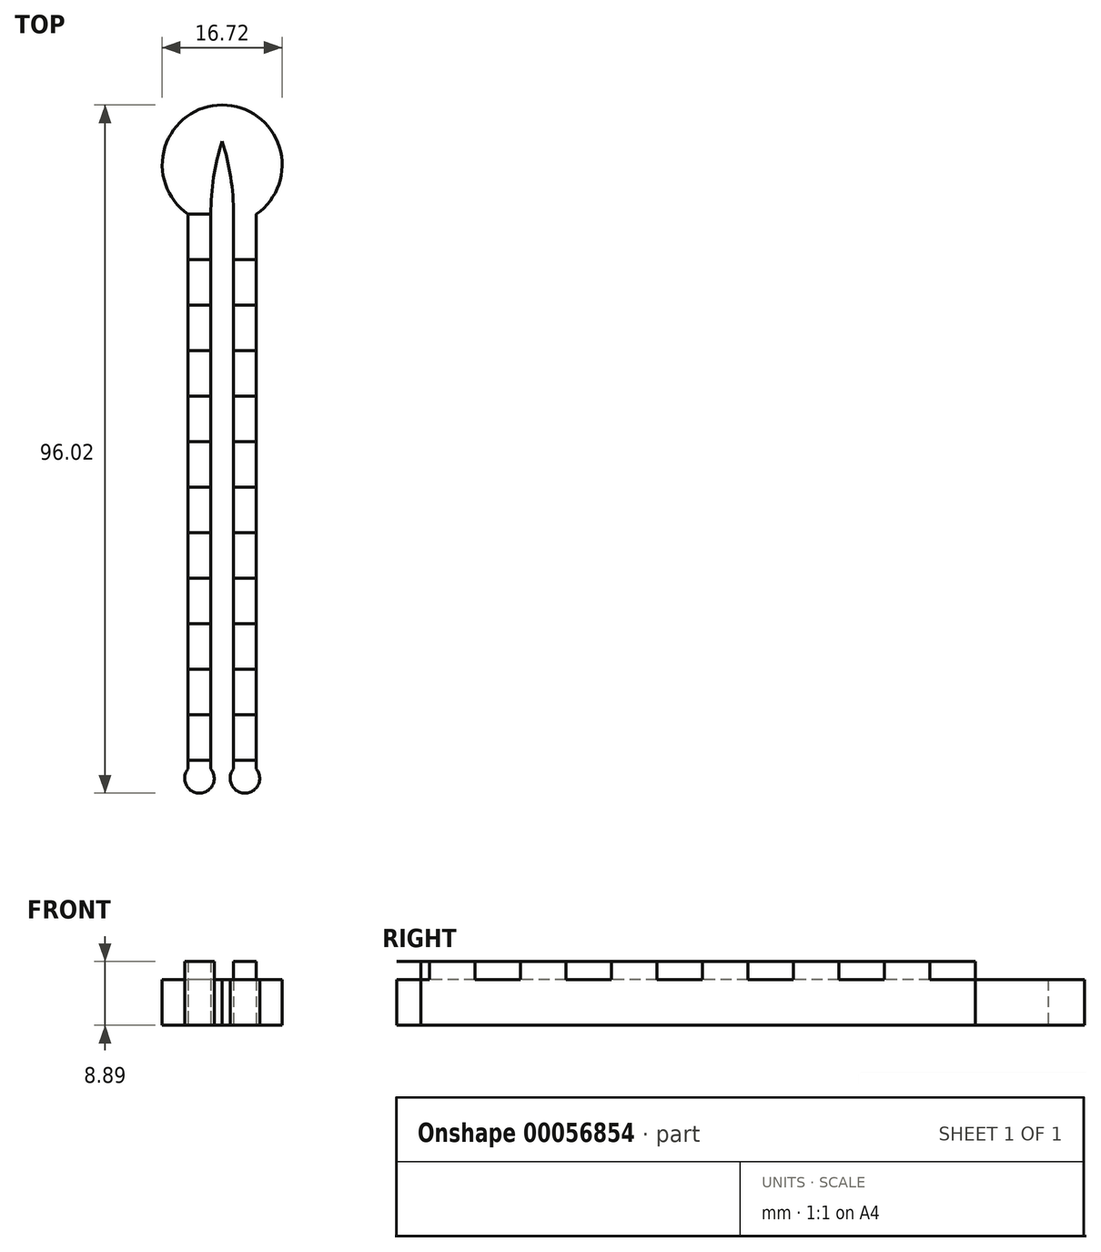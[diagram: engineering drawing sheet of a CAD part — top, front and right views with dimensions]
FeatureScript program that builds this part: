
annotation { "Feature Type Name" : "Feature", "Feature Type Description" : "" }
export const myFeature = defineFeature(function(context is Context, id is Id, definition is map)
    precondition{}
    {
        {
            var Q0;
            Q0=qCreatedBy(makeId("Top.planeOp"),FACE);
            var sketch = newSketch(context, id + "F0", { "sketchPlane" : qUnion([Q0])});
            skLineSegment(sketch, "E0", {"start": v(0, 31.42) * mm, "end": v(0, -56.14) * mm, "construction": true});
            skLineSegment(sketch, "E1.0", {"start": v(-1.59, 21.26) * mm, "end": v(-1.59, -56.14) * mm, "construction": true});
            skLineSegment(sketch, "E2", {"start": v(0, 31.42) * mm, "end": v(-38.89, 31.42) * mm, "construction": true});
            skLineSegment(sketch, "E3.0", {"start": v(0, -54.94) * mm, "end": v(-38.89, -54.94) * mm, "construction": true});
            skLineSegment(sketch, "E4.0", {"start": v(0, 21.26) * mm, "end": v(-38.89, 21.26) * mm, "construction": true});
            skArc(sketch, "E5", {"start": v(0, 31.42) * mm, "mid": v(-1.19, 26.4) * mm, "end": v(-1.59, 21.26) * mm});
            skLineSegment(sketch, "E6.0", {"start": v(-4.76, 21.26) * mm, "end": v(-4.76, -56.14) * mm});
            skLineSegment(sketch, "E7.0", {"start": v(0, 36.5) * mm, "end": v(-38.89, 36.5) * mm, "construction": true});
            skArc(sketch, "E8", {"start": v(0, 36.5) * mm, "mid": v(-7.98, 30.63) * mm, "end": v(-4.76, 21.26) * mm});
            skArc(sketch, "E9", {"start": v(-4.76, -56.14) * mm, "mid": v(-3.17, -59.52) * mm, "end": v(-1.59, -56.14) * mm});
            skLineSegment(sketch, "E10", {"start": v(-1.59, 21.26) * mm, "end": v(-1.59, -56.14) * mm});
            skLineSegment(sketch, "E11", {"start": v(0, 36.5) * mm, "end": v(0, 31.42) * mm});
            skArc(sketch, "E12.MirrorCS", {"start": v(0, 36.5) * mm, "mid": v(7.98, 30.63) * mm, "end": v(4.76, 21.26) * mm});
            skArc(sketch, "E13.MirrorCS", {"start": v(0, 31.42) * mm, "mid": v(1.19, 26.4) * mm, "end": v(1.59, 21.26) * mm});
            skLineSegment(sketch, "E14.MirrorCS", {"start": v(1.59, 21.26) * mm, "end": v(1.59, -56.14) * mm});
            skLineSegment(sketch, "E15.MirrorCS", {"start": v(4.76, 21.26) * mm, "end": v(4.76, -56.14) * mm});
            skArc(sketch, "E16.MirrorCS", {"start": v(4.76, -56.14) * mm, "mid": v(3.17, -59.52) * mm, "end": v(1.59, -56.14) * mm});
            skSolve(sketch);
        }
        {
            var Q0;
            Q0=makeQuery(id+"F0.imprint","IMPRINT",FACE,{"disambiguationData":[TD([[makeQuery(id+"F0.imprint","IMPRINT",EDGE,{"derivedFrom":sQuery(id+"F0.wireOp",EDGE,"E11")}),1.0]])]});
            var Q1;
            Q1=makeQuery(id+"F0.imprint","IMPRINT",FACE,{"disambiguationData":[TD([[makeQuery(id+"F0.imprint","IMPRINT",EDGE,{"derivedFrom":sQuery(id+"F0.wireOp",EDGE,"E5")}),-1.0]])]});
            extrude(context, id + "F1", {"entities" : qUnion([Q0, Q1]), "depth" : 6.35 * mm});
        }
        {
            var Q0;
            Q0=makeQuery(id+"F1.opExtrude","CAP_FACE",FACE,{"disambiguationData":[OSD([sQuery(id+"F0.wireOp",EDGE,"E5"),sQuery(id+"F0.wireOp",EDGE,"E6.0"),sQuery(id+"F0.wireOp",EDGE,"E8"),sQuery(id+"F0.wireOp",EDGE,"E9"),sQuery(id+"F0.wireOp",EDGE,"E10"),sQuery(id+"F0.wireOp",EDGE,"E12.MirrorCS"),sQuery(id+"F0.wireOp",EDGE,"E13.MirrorCS"),sQuery(id+"F0.wireOp",EDGE,"E14.MirrorCS"),sQuery(id+"F0.wireOp",EDGE,"E15.MirrorCS"),sQuery(id+"F0.wireOp",EDGE,"E16.MirrorCS")])],"isStart":false});
            var sketch = newSketch(context, id + "F2", { "sketchPlane" : qUnion([Q0])});
            skLineSegment(sketch, "E17.0", {"start": v(-1.59, 21.26) * mm, "end": v(-4.76, 21.26) * mm});
            skLineSegment(sketch, "E18.0", {"start": v(-4.76, 21.26) * mm, "end": v(-4.76, -56.14) * mm, "construction": true});
            skLineSegment(sketch, "E19.0", {"start": v(-1.59, 21.26) * mm, "end": v(-1.59, -56.14) * mm, "construction": true});
            skPoint(sketch, "E20.orphan", {"position": v(-38.89, 21.26) * mm});
            skPoint(sketch, "E21.orphan", {"position": v(0, 21.26) * mm});
            skLineSegment(sketch, "E22.0", {"start": v(-1.59, 14.91) * mm, "end": v(-4.76, 14.91) * mm});
            skLineSegment(sketch, "E23.0", {"start": v(-1.59, 8.56) * mm, "end": v(-4.76, 8.56) * mm});
            skLineSegment(sketch, "E24.0", {"start": v(-1.59, 2.21) * mm, "end": v(-4.76, 2.21) * mm});
            skLineSegment(sketch, "E25.0", {"start": v(-1.59, -4.14) * mm, "end": v(-4.76, -4.14) * mm});
            skLineSegment(sketch, "E26.0", {"start": v(-1.59, -10.49) * mm, "end": v(-4.76, -10.49) * mm});
            skLineSegment(sketch, "E27.0", {"start": v(-1.59, -16.84) * mm, "end": v(-4.76, -16.84) * mm});
            skLineSegment(sketch, "E28.MirrorCS", {"start": v(-1.59, -23.19) * mm, "end": v(-4.76, -23.19) * mm});
            skLineSegment(sketch, "E29.MirrorCS", {"start": v(-1.59, -29.54) * mm, "end": v(-4.76, -29.54) * mm});
            skLineSegment(sketch, "E30.MirrorCS", {"start": v(-1.59, -42.24) * mm, "end": v(-4.76, -42.24) * mm});
            skLineSegment(sketch, "E31.MirrorCS", {"start": v(-1.59, -54.94) * mm, "end": v(-4.76, -54.94) * mm});
            skLineSegment(sketch, "E32.MirrorCS", {"start": v(-1.59, -35.89) * mm, "end": v(-4.76, -35.89) * mm});
            skLineSegment(sketch, "E33.MirrorCS", {"start": v(-1.59, -48.59) * mm, "end": v(-4.76, -48.59) * mm});
            skLineSegment(sketch, "E34.MirrorCS", {"start": v(1.59, 21.26) * mm, "end": v(4.76, 21.26) * mm});
            skLineSegment(sketch, "E35.MirrorCS", {"start": v(1.59, 14.91) * mm, "end": v(4.76, 14.91) * mm});
            skLineSegment(sketch, "E36.MirrorCS", {"start": v(1.59, 8.56) * mm, "end": v(4.76, 8.56) * mm});
            skLineSegment(sketch, "E37.MirrorCS", {"start": v(1.59, 2.21) * mm, "end": v(4.76, 2.21) * mm});
            skLineSegment(sketch, "E38.MirrorCS", {"start": v(1.59, -4.14) * mm, "end": v(4.76, -4.14) * mm});
            skLineSegment(sketch, "E39.MirrorCS", {"start": v(1.59, -54.94) * mm, "end": v(4.76, -54.94) * mm});
            skLineSegment(sketch, "E40.MirrorCS", {"start": v(1.59, -48.59) * mm, "end": v(4.76, -48.59) * mm});
            skLineSegment(sketch, "E41.MirrorCS", {"start": v(1.59, -42.24) * mm, "end": v(4.76, -42.24) * mm});
            skLineSegment(sketch, "E42.MirrorCS", {"start": v(1.59, -35.89) * mm, "end": v(4.76, -35.89) * mm});
            skLineSegment(sketch, "E43.MirrorCS", {"start": v(1.59, -29.54) * mm, "end": v(4.76, -29.54) * mm});
            skLineSegment(sketch, "E44.MirrorCS", {"start": v(1.59, -23.19) * mm, "end": v(4.76, -23.19) * mm});
            skLineSegment(sketch, "E45.MirrorCS", {"start": v(1.59, -16.84) * mm, "end": v(4.76, -16.84) * mm});
            skLineSegment(sketch, "E46.MirrorCS", {"start": v(1.59, -10.49) * mm, "end": v(4.76, -10.49) * mm});
            skSolve(sketch);
        }
        {
            var Q0;
            {var subQ0=sQuery(id+"F2.wireOp",EDGE,"E17.0");Q0=makeQuery(id+"F2.imprint","IMPRINT",FACE,{"disambiguationData":[TD([[makeQuery(id+"F2.imprint","IMPRINT",EDGE,{"derivedFrom":subQ0}),1.0]])]});}
            var Q1;
            {var subQ0=sQuery(id+"F2.wireOp",EDGE,"E35.MirrorCS");Q1=makeQuery(id+"F2.imprint","IMPRINT",FACE,{"disambiguationData":[TD([[makeQuery(id+"F2.imprint","IMPRINT",EDGE,{"derivedFrom":subQ0}),-1.0]])]});}
            var Q2;
            {var subQ0=sQuery(id+"F2.wireOp",EDGE,"E23.0");Q2=makeQuery(id+"F2.imprint","IMPRINT",FACE,{"disambiguationData":[TD([[makeQuery(id+"F2.imprint","IMPRINT",EDGE,{"derivedFrom":subQ0}),1.0]])]});}
            var Q3;
            {var subQ0=sQuery(id+"F2.wireOp",EDGE,"E37.MirrorCS");Q3=makeQuery(id+"F2.imprint","IMPRINT",FACE,{"disambiguationData":[TD([[makeQuery(id+"F2.imprint","IMPRINT",EDGE,{"derivedFrom":subQ0}),-1.0]])]});}
            var Q4;
            {var subQ0=sQuery(id+"F2.wireOp",EDGE,"E25.0");Q4=makeQuery(id+"F2.imprint","IMPRINT",FACE,{"disambiguationData":[TD([[makeQuery(id+"F2.imprint","IMPRINT",EDGE,{"derivedFrom":subQ0}),1.0]])]});}
            var Q5;
            {var subQ0=sQuery(id+"F2.wireOp",EDGE,"E45.MirrorCS");Q5=makeQuery(id+"F2.imprint","IMPRINT",FACE,{"disambiguationData":[TD([[makeQuery(id+"F2.imprint","IMPRINT",EDGE,{"derivedFrom":subQ0}),1.0]])]});}
            var Q6;
            {var subQ0=sQuery(id+"F2.wireOp",EDGE,"E27.0");Q6=makeQuery(id+"F2.imprint","IMPRINT",FACE,{"disambiguationData":[TD([[makeQuery(id+"F2.imprint","IMPRINT",EDGE,{"derivedFrom":subQ0}),1.0]])]});}
            var Q7;
            {var subQ0=sQuery(id+"F2.wireOp",EDGE,"E43.MirrorCS");Q7=makeQuery(id+"F2.imprint","IMPRINT",FACE,{"disambiguationData":[TD([[makeQuery(id+"F2.imprint","IMPRINT",EDGE,{"derivedFrom":subQ0}),1.0]])]});}
            var Q8;
            {var subQ0=sQuery(id+"F2.wireOp",EDGE,"E29.MirrorCS");Q8=makeQuery(id+"F2.imprint","IMPRINT",FACE,{"disambiguationData":[TD([[makeQuery(id+"F2.imprint","IMPRINT",EDGE,{"derivedFrom":subQ0}),1.0]])]});}
            var Q9;
            {var subQ0=sQuery(id+"F2.wireOp",EDGE,"E41.MirrorCS");Q9=makeQuery(id+"F2.imprint","IMPRINT",FACE,{"disambiguationData":[TD([[makeQuery(id+"F2.imprint","IMPRINT",EDGE,{"derivedFrom":subQ0}),1.0]])]});}
            var Q10;
            {var subQ0=sQuery(id+"F2.wireOp",EDGE,"E30.MirrorCS");Q10=makeQuery(id+"F2.imprint","IMPRINT",FACE,{"disambiguationData":[TD([[makeQuery(id+"F2.imprint","IMPRINT",EDGE,{"derivedFrom":subQ0}),1.0]])]});}
            var Q11;
            {var subQ0=sQuery(id+"F2.wireOp",EDGE,"E39.MirrorCS");Q11=makeQuery(id+"F2.imprint","IMPRINT",FACE,{"disambiguationData":[TD([[makeQuery(id+"F2.imprint","IMPRINT",EDGE,{"derivedFrom":subQ0}),1.0]])]});}
            var Q12;
            {var subQ0=sQuery(id+"F2.wireOp",EDGE,"E31.MirrorCS");Q12=makeQuery(id+"F2.imprint","IMPRINT",FACE,{"disambiguationData":[TD([[makeQuery(id+"F2.imprint","IMPRINT",EDGE,{"derivedFrom":subQ0}),1.0]])]});}
            extrude(context, id + "F3", {"entities" : qUnion([Q0, Q1, Q2, Q3, Q4, Q5, Q6, Q7, Q8, Q9, Q10, Q11, Q12]), "operationType" : NewBodyOperationType.ADD, "depth" : 2.54 * mm});
        }
    });
